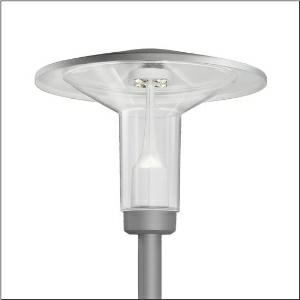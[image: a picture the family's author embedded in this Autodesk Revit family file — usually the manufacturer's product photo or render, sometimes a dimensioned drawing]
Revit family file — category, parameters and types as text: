
# Revit family: laterne_iq___p1_0a_5xa5255nf14h_4412
name_source: partatom
category: Lighting Fixtures
units: mm (PartAtom-declared; Revit-internal decimal feet)

## family parameters
Cut with Voids When Loaded = No
Host = Face
Light Source = No
Part Type = Normal
Room Calculation Point = No
Round Connector Dimension = Use Diameter
Shared = No

## types (1)
- --- (1 x LED, 1510 lm, 11.8 W, 2700K)
    Apparent Load = 12 VA
    CIE Flux Codes = 35 64 91 96 100
    Color Rendering = 70
    Color Temperature = 2700K
    Default Elevation = 1800 mm
    Description = Lantern iQ, mast luminaire, Module 540 iQ-SR, primary light control with 3 zone facetted reflector, of plastic, silver coated, highly specular, structured, primary optical cover: cover, of PMMA, transparent, light distribution: P1.0a, light emission: direct distribution, primary light characteristic: strongly asymmetric, installation type: post-top, LED, High Power LED, rated luminous flux: 1.510lm, luminous efficacy: 128lm/W, light colour: 727, colour temperature: 2700K, control gear: iQ Street-Remote, control: pre-setting: logarithmic dimming characteristic, Street-Remote, Auto-Match, Temp-Guard, Lumen-Switch, Night-Set, Smart-Wire, Light-Fading, Desk-Remote (wireless, voltage-free reading and setting of iQ features in the workshop via application-optimized NFC function/RFID function), optimised constant luminous flux control (CLO 2.0), with terminal, 6-pole, max. 2.5mm², mains connection: 230..240V, AC, 50/60Hz, start of lifetime: 12W, end of service life: 12W, reduction: 6W, luminaire housing, upper part, of glass-fibre reinforced polyester, coated, Siteco® metallic grey (DB 702S), diameter: 750mm, height: 583mm, spigot size: d x l = 76 x 70mm (post-top) | with reducer (optional accessory) 60 x 70mm, mounting height: 3..5m, post-top mast mounting element, of diecast aluminium, coated, Siteco® metallic grey (DB 702S), Module 540 iQ-SR, traffic white (RAL 9016), equipment: standard, protection rating (complete): IP65, insulation class (complete): insulation class II (safety insulation), certification: CE, ENEC, VDE, packaging unit: 1 piece

Light Distribution: P1.0a
    Height = 583 mm
    Lamp = 1 x LED
    Lamp Light Flux = 1510 lm
    Lamp Power = 11.8 W
    Lamp count = 1
    Length = 750 mm
    Luminous efficacy = 128 lm/W
    Manufacturer = Siteco
    ModVariant = No
    Model = 5XA5255NF14H
    Number of Poles = 1
    OnlyDefault = Yes
    Power Factor = 1
    Product Name = Laterne iQ | P1.0a
    Product group = mast luminaire | pylon top
    ProductGroupID = 6100
    Protection Class = Protection class II
    Protection Degree = IP 65
    RLX_Detail_Level = 1
    RLX_Emergency_Light_Flux = 0 lm
    RLX_Emergency_Type = 0
    RLX_Emergency_Type_DB = No
    RlxData = <blob elided: 73969 chars, md5=a0e123fb>
    Socket = socket
    Standby Power = 0 W
    System Light Flux = 1510 lm
    System Power = 12 W
    Type Comments = factory setting: luminous flux: 100 % | dim-lin: 254 | 472 mA
    Type Image = l_1006050.jpg
    URL = http://relux.com
    VarID = @adj_174855
    Voltage = 0 V
    Weight = 0.00 kg
    Width = 0 mm  [stored 0 ft]

note: [stored X ft] marks values corroborated as IEEE doubles in the binary element streams (Revit-internal decimal feet)

## geometry (parser evidence)
native form markers: Blend x4, Sweep x9
no freeform markers — native parametric forms only
